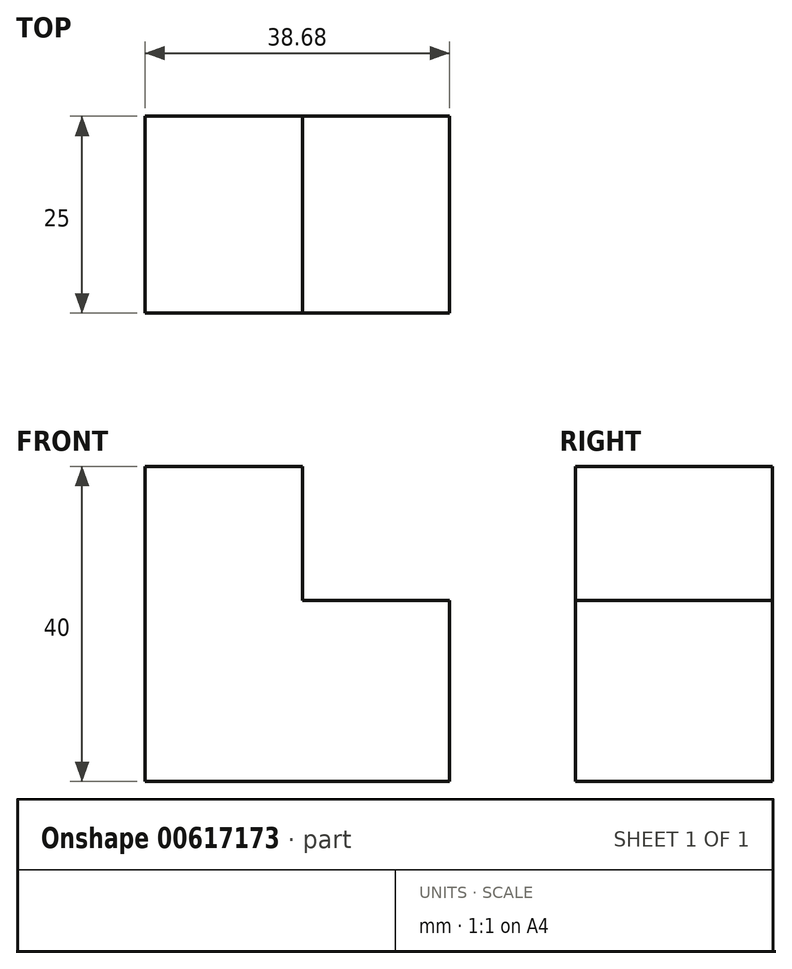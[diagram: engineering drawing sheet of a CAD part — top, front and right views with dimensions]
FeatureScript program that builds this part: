
annotation { "Feature Type Name" : "Feature", "Feature Type Description" : "" }
export const myFeature = defineFeature(function(context is Context, id is Id, definition is map)
    precondition{}
    {
        {
            var Q0;
            Q0=qCreatedBy(makeId("Front.planeOp"),FACE);
            var sketch = newSketch(context, id + "F0", { "sketchPlane" : qUnion([Q0])});
            skLineSegment(sketch, "E0", {"start": v(-46.8, 53.96) * mm, "end": v(-46.8, 13.96) * mm});
            skLineSegment(sketch, "E1", {"start": v(-46.8, 53.96) * mm, "end": v(-26.8, 53.96) * mm});
            skLineSegment(sketch, "E2", {"start": v(-26.8, 53.96) * mm, "end": v(-26.8, 13.96) * mm});
            skLineSegment(sketch, "E3", {"start": v(-26.8, 13.96) * mm, "end": v(-46.8, 13.96) * mm});
            skLineSegment(sketch, "E4", {"start": v(-26.8, 36.91) * mm, "end": v(-8.1, 36.91) * mm});
            skLineSegment(sketch, "E5", {"start": v(-8.1, 36.91) * mm, "end": v(-8.1, 13.96) * mm});
            skLineSegment(sketch, "E6", {"start": v(-26.8, 13.96) * mm, "end": v(-8.1, 13.96) * mm});
            skSolve(sketch);
        }
        {
            var Q0;
            {var subQ2=sQuery(id+"F0.wireOp",EDGE,"E4");Q0=makeQuery(id+"F0.imprint","IMPRINT",FACE,{"disambiguationData":[TD([[makeQuery(id+"F0.imprint","IMPRINT",EDGE,{"derivedFrom":subQ2}),-1.0]])]});}
            var Q1;
            Q1=makeQuery(id+"F0.imprint","IMPRINT",FACE,{"disambiguationData":[TD([[makeQuery(id+"F0.imprint","IMPRINT",EDGE,{"derivedFrom":sQuery(id+"F0.wireOp",EDGE,"E0")}),1.0]])]});
            extrude(context, id + "F1", {"entities" : qUnion([Q0, Q1]), "depth" : 25 * mm, "offsetDistance" : 25 * mm});
        }
    });
